# Revit family: Excitech_Delmatic_LightingControlModule_163A1-MetroDaliBroadcastModule
name_source: partatom
category: Electrical Equipment
revit_build: Autodesk Revit 2013 (Build: 20130531_2115(x64)
units: mm (PartAtom-declared; Revit-internal decimal feet)

## types (1)
- Excitech_Delmatic_LightingControlModule_163A1-MetroDaliBroadcastModule
    AssetType = Fixed
    BIMObjectName = Excitech_Delmatic_LightingControlModule_MetroDaliBroadcastModule_163A1
    Category = Ac-45-65-47
    Color = RAL 9002
    Constituents = Modular unit comprises metal enclosure, module Dali electronics, plug-in Lon/BACnet intelligence capsule.
    Default Elevation = 0 mm  [stored 0 ft]
    Description = The Dali Broadcast Module provides fully addressable control with individual switching, dimming and monitoring of twelve Dali channels and is used in areas such as cores where total flexibility is not required.  

The Dali Broadcast Module requires no on-site addressing.
    DurationUnit = year
    ExpectedLife = 20
    Features = 12 individually pre-addressed DALI channel outputs.
UP to 40 luminaires per channel.
Dali Without Addressing avoids onsite addressing of DALI ballasts.
DALI lamp and ballast failure monitoring on a channel basis.
Individual DALI emergency light testing and monitoring.
DALI sensors, switches and emergency devices connect to DALI channel buswire.
    Finish = Moulded enclosure
    IfcExportAs = IfcElectricDistributionPoint
    IfcExportType = NOTDEFINED
    IfcTypeObject = IfcElectricDistributionPoint
    IsMain = False
    MCB Rating = 10 A
    Mains Type = Single phase
    Manufacturer = Delmatic Lighting Management
    ManufacturerURL = www.delmatic.com/contact
    Material = Flame retardant ABS enclosure
    Model = 204A1, Metro Dali Broadcast Module
    ModelNumber = 204A1
    ModelReference = Dali Broadcast Module 204A1
    NBSDescription = Hard wired general lighting system
    NBSReference = 70-80-35/110
    Name = Dali Broadcast Module
    NominalHeight = 70 mm  [stored 0.229659 ft]
    NominalLength = 330 mm  [stored 1.08268 ft]
    NominalWidth = 190 mm  [stored 0.62336 ft]
    ProductInformation = http://www.delmatic.com
    Revision = 3
    Shape = Rectangular
    Size = Compact
    SustainabilityPerformance = The module is designed to maximise sustainability through the use of modular electronics which enable products to be upgraded with 90% of the unit being re-used.
    URL = http://www.delmatic.com
    Uniclass1 = G543
    Uniclass2 = Ac-45-65-47
    UnitMaterial = ABS Plastic
    Version = 4
    Voltage = 230
    WarrantyDescription = Warranty allows for free of charge factory repair or replacement of any parts proving to be faulty provided they have been installed and operated correctly.
    WarrantyDurationLabor = 1
    WarrantyDurationParts = 8
    WarrantyDurationUnit = year
    Wattage = 9

note: [stored X ft] marks values corroborated as IEEE doubles in the binary element streams (Revit-internal decimal feet)

## geometry (parser evidence)
native form markers: Blend x4, Sweep x3
no freeform markers — native parametric forms only
